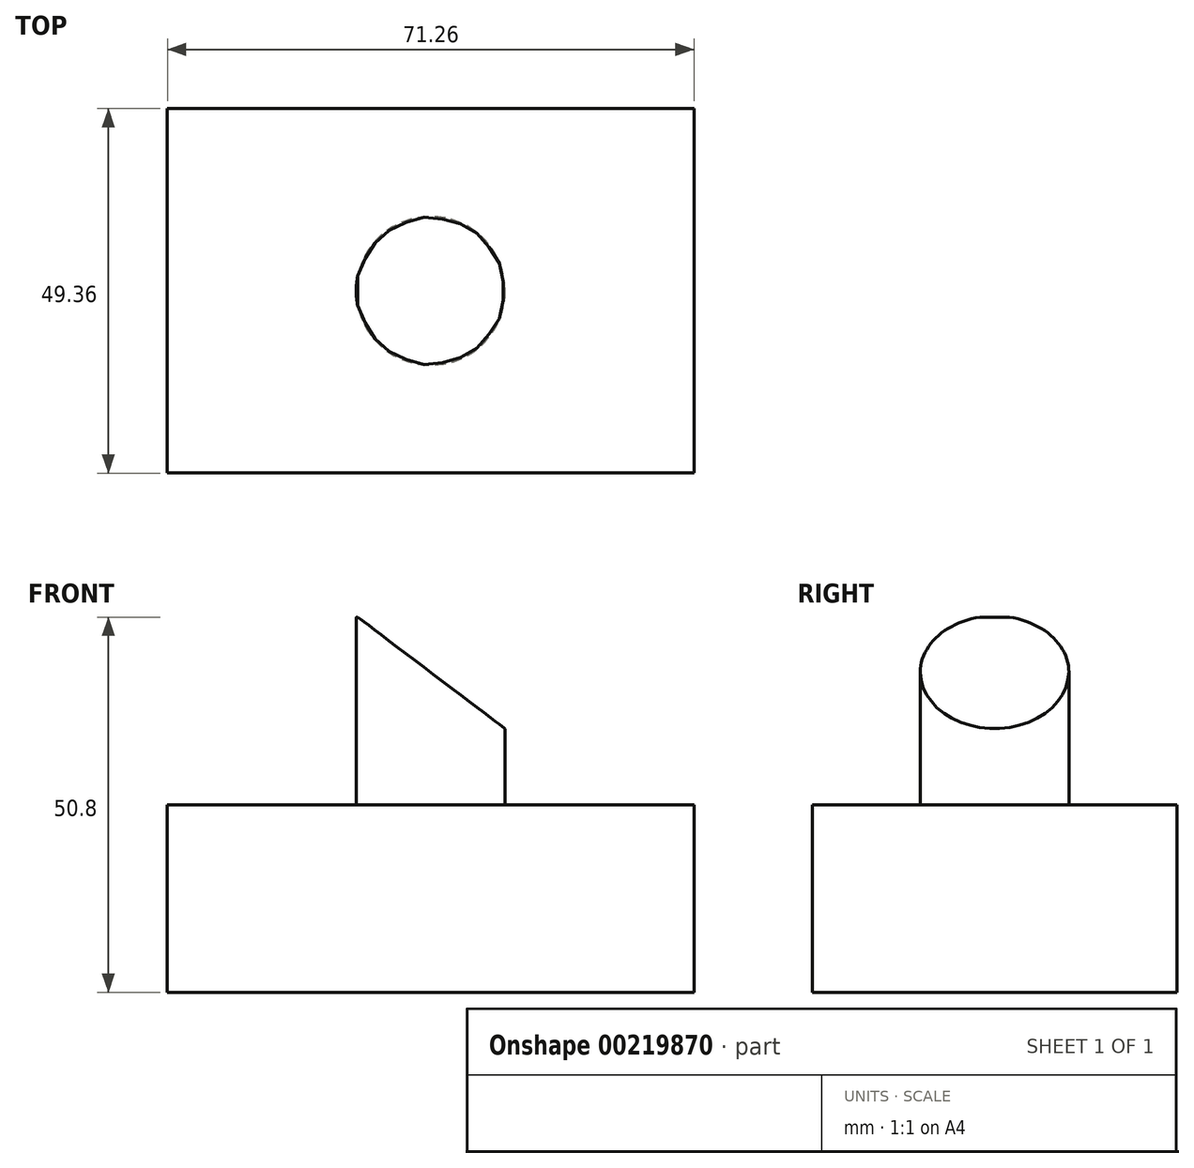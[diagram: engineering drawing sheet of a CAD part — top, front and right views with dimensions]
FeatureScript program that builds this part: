
annotation { "Feature Type Name" : "Feature", "Feature Type Description" : "" }
export const myFeature = defineFeature(function(context is Context, id is Id, definition is map)
    precondition{}
    {
        {
            var Q0;
            Q0=qCreatedBy(makeId("Top.planeOp"),FACE);
            var sketch = newSketch(context, id + "F0", { "sketchPlane" : qUnion([Q0])});
            skLineSegment(sketch, "E0.bottom", {"start": v(35.63, 24.68) * mm, "end": v(-35.63, 24.68) * mm});
            skLineSegment(sketch, "E0.top", {"start": v(35.63, -24.68) * mm, "end": v(-35.63, -24.68) * mm});
            skLineSegment(sketch, "E0.left", {"start": v(35.63, 24.68) * mm, "end": v(35.63, -24.68) * mm});
            skLineSegment(sketch, "E0.right", {"start": v(-35.63, 24.68) * mm, "end": v(-35.63, -24.68) * mm});
            skPoint(sketch, "E0.middle", {"position": v(0, 0) * mm});
            skSolve(sketch);
        }
        {
            var Q0;
            Q0 = qSketchRegion(id + "F0", true);
            extrude(context, id + "F1", {"entities" : qUnion([Q0]), "depth" : 25.4 * mm});
        }
        {
            var Q0;
            Q0=makeQuery(id+"F1.opExtrude","CAP_FACE",FACE,{"disambiguationData":[OSD([sQuery(id+"F0.wireOp",EDGE,"E0.bottom"),sQuery(id+"F0.wireOp",EDGE,"E0.top"),sQuery(id+"F0.wireOp",EDGE,"E0.left"),sQuery(id+"F0.wireOp",EDGE,"E0.right")])],"isStart":false});
            var sketch = newSketch(context, id + "F2", { "sketchPlane" : qUnion([Q0])});
            skCircle(sketch, "E1", {"center": v(0, 0) * mm, "radius": 10.07 * mm});
            skSolve(sketch);
        }
        {
            var Q0;
            Q0=makeQuery(id+"F2.imprint","IMPRINT",FACE,{"disambiguationData":[TD([[makeQuery(id+"F2.imprint","IMPRINT",EDGE,{"derivedFrom":sQuery(id+"F2.wireOp",EDGE,"E1")}),1.0]])]});
            extrude(context, id + "F3", {"entities" : qUnion([Q0]), "operationType" : NewBodyOperationType.ADD, "depth" : 25.4 * mm});
        }
        {
            var Q0;
            Q0=makeQuery(id+"F1.opExtrude","SWEPT_FACE",FACE,{"disambiguationData":[OSD([sQuery(id+"F0.wireOp",EDGE,"E0.top")])]});
            var sketch = newSketch(context, id + "F4", { "sketchPlane" : qUnion([Q0])});
            skLineSegment(sketch, "E2", {"start": v(-10.06, 50.95) * mm, "end": v(15.78, 31.36) * mm});
            skLineSegment(sketch, "E3", {"start": v(15.78, 31.36) * mm, "end": v(15.78, 50.95) * mm});
            skLineSegment(sketch, "E4", {"start": v(15.78, 50.95) * mm, "end": v(-10.06, 50.95) * mm});
            skSolve(sketch);
        }
        {
            var Q0;
            Q0=makeQuery(id+"F4.imprint","IMPRINT",FACE,{"disambiguationData":[TD([[makeQuery(id+"F4.imprint","IMPRINT",EDGE,{"derivedFrom":sQuery(id+"F4.wireOp",EDGE,"E2")}),1.0]])]});
            extrude(context, id + "F5", {"entities" : qUnion([Q0]), "operationType" : NewBodyOperationType.REMOVE, "oppositeDirection" : true, "depth" : 46.23 * mm});
        }
    });
